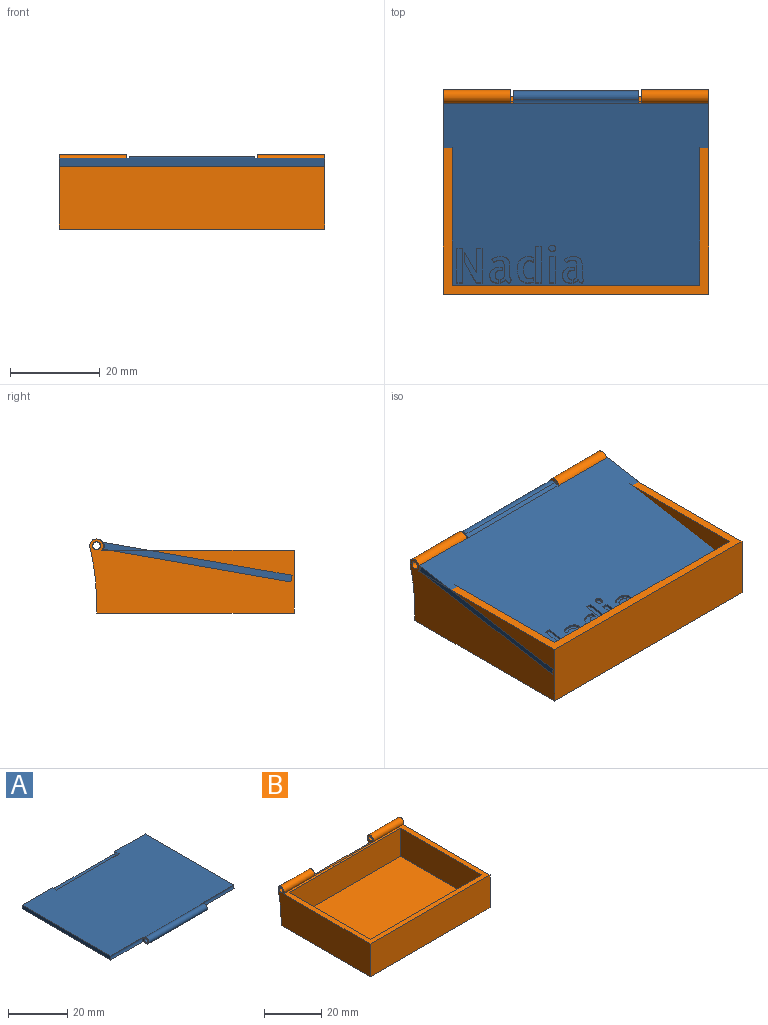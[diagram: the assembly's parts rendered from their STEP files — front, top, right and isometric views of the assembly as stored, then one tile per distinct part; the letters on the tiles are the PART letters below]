
ASSEMBLY  parts=2 mates=1
PART A: 187 faces, bbox 59x45.3x2.5 mm
  f0: plane 59x42.85mm, normal (0,0,1), area 2451.9mm2, adj f2,f4,f5,f6,f7,f8,f9,f10
  f1: plane 59x42.56mm, normal (0,0,-1), area 2423.8mm2, adj f2,f5,f6,f9,f10,f11,f12,f13
  f2: plane 42.56x1.5mm, normal (1,0,0), area 63.5mm2, adj f0,f1,f6,f10
  f3: cylinder r=0.82mm len=28mm, axis (-1,0,0), area 145.1mm2, adj f7,f8
  f4: cylinder r=1.25mm len=28mm, axis (-1,0,0), area 162.6mm2, adj f0,f7,f8,f186
  f5: plane 42.56x1.5mm, normal (-1,0,0), area 63.5mm2, adj f0,f1,f6,f9
  f6: plane 59x1.5mm, normal (0,1,0), area 66.6mm2, adj f0,f1,f2,f5,f182,f183,f185
  f7: plane 3x2.5mm, normal (-1,0,0), area 3.6mm2, adj f0,f3,f4,f9,f186
  f8: plane 3x2.5mm, normal (1,0,0), area 3.6mm2, adj f0,f3,f4,f10,f186
  f9: cylinder r=1.75mm len=15.5mm, axis (1,0,0), area 24.4mm2, adj f0,f1,f5,f7
  f10: cylinder r=1.75mm len=15.5mm, axis (-1,0,0), area 24.4mm2, adj f0,f1,f2,f8
  f11: plane 1.29x0.5mm, normal (0,1,0), area 0.6mm2, adj f1,f12,f17,f18
  f12: plane 5.36x0.5mm, normal (1,0,0), area 2.7mm2, adj f1,f11,f13,f18
  f13: plane 4.61x2.62mm, normal (-0.87,0.49,0), area 2.7mm2, adj f1,f12,f14,f18
  f14: plane 2.43x0.5mm, normal (1,0,0), area 1.2mm2, adj f1,f13,f15,f18
  f15: plane 4.6x2.62mm, normal (0.87,-0.49,0), area 2.6mm2, adj f1,f14,f16,f18
  f16: plane 1.29x0.5mm, normal (0,-1,0), area 0.6mm2, adj f1,f15,f17,f18
  f17: plane 7.78x0.5mm, normal (-1,0,0), area 3.9mm2, adj f1,f11,f16,f18
  f18: plane 7.78x3.9mm, normal (0,0,-1), area 16.3mm2, adj f11,f12,f13,f14,f15,f16,f17
  f19: extruded ~0.5x0.25mm, area 0.1mm2, adj f1,f20,f53,f54
  f20: plane 1.46x0.5mm, normal (-1,0,0), area 0.7mm2, adj f1,f19,f21,f54
  f21: extruded ~0.74x0.5mm, area 0.4mm2, adj f1,f20,f22,f54
  f22: extruded ~0.74x0.5mm, area 0.4mm2, adj f1,f21,f23,f54
  f23: extruded ~0.62x0.5mm, area 0.3mm2, adj f1,f22,f24,f54
  f24: extruded ~0.5x0.43mm, area 0.3mm2, adj f1,f23,f25,f54
  f25: extruded ~0.55x0.5mm, area 0.3mm2, adj f1,f24,f26,f54
  f26: extruded ~0.62x0.5mm, area 0.3mm2, adj f1,f25,f27,f54
  f27: extruded ~0.67x0.5mm, area 0.3mm2, adj f1,f26,f28,f54
  f28: extruded ~0.6x0.5mm, area 0.3mm2, adj f1,f27,f29,f54
  f29: extruded ~0.5x0.49mm, area 0.3mm2, adj f1,f28,f30,f54
  f30: extruded ~0.5x0.32mm, area 0.2mm2, adj f1,f29,f31,f54
  f31: plane 0.73x0.5mm, normal (0.84,-0.55,0), area 0.4mm2, adj f1,f30,f32,f54
  f32: extruded ~0.5x0.2mm, area 0.1mm2, adj f1,f31,f33,f54
  f33: extruded ~0.5x0.31mm, area 0.2mm2, adj f1,f32,f34,f54
  f34: extruded ~0.5x0.38mm, area 0.2mm2, adj f1,f33,f35,f54
  f35: extruded ~0.5x0.44mm, area 0.2mm2, adj f1,f34,f36,f54
  f36: extruded ~0.5x0.44mm, area 0.2mm2, adj f1,f35,f37,f54
  f37: extruded ~0.5x0.31mm, area 0.2mm2, adj f1,f36,f38,f54
  f38: extruded ~0.5x0.45mm, area 0.2mm2, adj f1,f37,f39,f54
  f39: extruded ~0.82x0.5mm, area 0.4mm2, adj f1,f38,f40,f54
  f40: plane 2.23x0.5mm, normal (1,0,0), area 1.1mm2, adj f1,f39,f41,f54
  f41: extruded ~0.5x0.36mm, area 0.3mm2, adj f1,f40,f42,f54
  f42: extruded ~0.5x0.46mm, area 0.3mm2, adj f1,f41,f43,f54
  f43: plane 0.8x0.5mm, normal (1,0,0), area 0.4mm2, adj f1,f42,f44,f54
  f44: extruded ~0.69x0.5mm, area 0.4mm2, adj f1,f43,f45,f54
  f45: extruded ~0.5x0.47mm, area 0.3mm2, adj f1,f44,f46,f54
  f46: extruded ~0.5x0.31mm, area 0.2mm2, adj f1,f45,f47,f54
  f47: extruded ~0.5x0.26mm, area 0.2mm2, adj f1,f46,f48,f54
  f48: extruded ~0.5x0.3mm, area 0.2mm2, adj f1,f47,f49,f54
  f49: extruded ~0.5x0.29mm, area 0.1mm2, adj f1,f48,f50,f54
  f50: plane 0.71x0.5mm, normal (-0.9,-0.43,0), area 0.4mm2, adj f1,f49,f51,f54
  f51: extruded ~0.5x0.19mm, area 0.1mm2, adj f1,f50,f52,f54
  f52: extruded ~0.5x0.31mm, area 0.2mm2, adj f1,f51,f53,f54
  f53: extruded ~0.5x0.33mm, area 0.2mm2, adj f1,f19,f52,f54
  f54: plane 6x4.39mm, normal (0,0,-1), area 9.9mm2, adj f19,f20,f21,f22,f23,f24,f25,f26
  f55: plane 8.2x0.5mm, normal (-1,0,0), area 4.1mm2, adj f1,f56,f59,f60
  f56: plane 1.29x0.5mm, normal (0,1,0), area 0.6mm2, adj f1,f55,f57,f60
  f57: plane 7.49x0.5mm, normal (1,0,0), area 3.7mm2, adj f1,f56,f58,f60
  f58: plane 0.71x0.5mm, normal (0.99,-0.1,0), area 0.4mm2, adj f1,f57,f59,f60
  f59: plane 1.21x0.5mm, normal (0,-1,0), area 0.6mm2, adj f1,f55,f58,f60
  f60: plane 8.2x1.29mm, normal (0,0,-1), area 10.5mm2, adj f55,f56,f57,f58,f59
  f61: extruded ~0.5x0.25mm, area 0.1mm2, adj f1,f62,f95,f96
  f62: plane 1.46x0.5mm, normal (-1,0,0), area 0.7mm2, adj f1,f61,f63,f96
  f63: extruded ~0.74x0.5mm, area 0.4mm2, adj f1,f62,f64,f96
  f64: extruded ~0.74x0.5mm, area 0.4mm2, adj f1,f63,f65,f96
  f65: extruded ~0.62x0.5mm, area 0.3mm2, adj f1,f64,f66,f96
  f66: extruded ~0.5x0.43mm, area 0.3mm2, adj f1,f65,f67,f96
  f67: extruded ~0.55x0.5mm, area 0.3mm2, adj f1,f66,f68,f96
  f68: extruded ~0.62x0.5mm, area 0.3mm2, adj f1,f67,f69,f96
  f69: extruded ~0.67x0.5mm, area 0.3mm2, adj f1,f68,f70,f96
  f70: extruded ~0.6x0.5mm, area 0.3mm2, adj f1,f69,f71,f96
  f71: extruded ~0.5x0.49mm, area 0.3mm2, adj f1,f70,f72,f96
  f72: extruded ~0.5x0.32mm, area 0.2mm2, adj f1,f71,f73,f96
  f73: plane 0.73x0.5mm, normal (0.84,-0.55,0), area 0.4mm2, adj f1,f72,f74,f96
  f74: extruded ~0.5x0.2mm, area 0.1mm2, adj f1,f73,f75,f96
  f75: extruded ~0.5x0.31mm, area 0.2mm2, adj f1,f74,f76,f96
  f76: extruded ~0.5x0.38mm, area 0.2mm2, adj f1,f75,f77,f96
  f77: extruded ~0.5x0.44mm, area 0.2mm2, adj f1,f76,f78,f96
  f78: extruded ~0.5x0.44mm, area 0.2mm2, adj f1,f77,f79,f96
  f79: extruded ~0.5x0.31mm, area 0.2mm2, adj f1,f78,f80,f96
  f80: extruded ~0.5x0.45mm, area 0.2mm2, adj f1,f79,f81,f96
  f81: extruded ~0.82x0.5mm, area 0.4mm2, adj f1,f80,f82,f96
  f82: plane 2.23x0.5mm, normal (1,0,0), area 1.1mm2, adj f1,f81,f83,f96
  f83: extruded ~0.5x0.36mm, area 0.3mm2, adj f1,f82,f84,f96
  f84: extruded ~0.5x0.46mm, area 0.3mm2, adj f1,f83,f85,f96
  f85: plane 0.8x0.5mm, normal (1,0,0), area 0.4mm2, adj f1,f84,f86,f96
  f86: extruded ~0.69x0.5mm, area 0.4mm2, adj f1,f85,f87,f96
  f87: extruded ~0.5x0.47mm, area 0.3mm2, adj f1,f86,f88,f96
  f88: extruded ~0.5x0.31mm, area 0.2mm2, adj f1,f87,f89,f96
  f89: extruded ~0.5x0.26mm, area 0.2mm2, adj f1,f88,f90,f96
  f90: extruded ~0.5x0.3mm, area 0.2mm2, adj f1,f89,f91,f96
  f91: extruded ~0.5x0.29mm, area 0.1mm2, adj f1,f90,f92,f96
  f92: plane 0.71x0.5mm, normal (-0.9,-0.43,0), area 0.4mm2, adj f1,f91,f93,f96
  f93: extruded ~0.5x0.19mm, area 0.1mm2, adj f1,f92,f94,f96
  f94: extruded ~0.5x0.31mm, area 0.2mm2, adj f1,f93,f95,f96
  f95: extruded ~0.5x0.33mm, area 0.2mm2, adj f1,f61,f94,f96
  f96: plane 6x4.39mm, normal (0,0,-1), area 9.9mm2, adj f61,f62,f63,f64,f65,f66,f67,f68
  f97: extruded ~0.71x0.5mm, area 0.4mm2, adj f1,f98,f115,f116
  f98: extruded ~0.55x0.5mm, area 0.3mm2, adj f1,f97,f99,f116
  f99: extruded ~0.5x0.33mm, area 0.2mm2, adj f1,f98,f100,f116
  f100: extruded ~0.5x0.43mm, area 0.2mm2, adj f1,f99,f101,f116
  f101: extruded ~0.5x0.44mm, area 0.2mm2, adj f1,f100,f102,f116
  f102: plane 0.5x0.23mm, normal (0,-1,0), area 0.1mm2, adj f1,f101,f103,f116
  f103: plane 0.75x0.5mm, normal (-1,0,0), area 0.4mm2, adj f1,f102,f104,f116
  f104: plane 0.5x0.46mm, normal (0,1,0), area 0.2mm2, adj f1,f103,f105,f116
  f105: extruded ~0.83x0.5mm, area 0.4mm2, adj f1,f104,f106,f116
  f106: extruded ~0.73x0.5mm, area 0.4mm2, adj f1,f105,f107,f116
  f107: extruded ~0.58x0.53mm, area 0.4mm2, adj f1,f106,f108,f116
  f108: extruded ~0.84x0.5mm, area 0.4mm2, adj f1,f107,f109,f116
  f109: extruded ~0.86x0.5mm, area 0.4mm2, adj f1,f108,f110,f116
  f110: extruded ~0.56x0.5mm, area 0.3mm2, adj f1,f109,f111,f116
  f111: extruded ~0.59x0.5mm, area 0.3mm2, adj f1,f110,f112,f116
  f112: extruded ~0.69x0.5mm, area 0.3mm2, adj f1,f111,f113,f116
  f113: extruded ~0.5x0.14mm, area 0.1mm2, adj f1,f112,f114,f116
  f114: plane 0.85x0.5mm, normal (-1,0,0), area 0.4mm2, adj f1,f113,f115,f116
  f115: extruded ~0.56x0.5mm, area 0.3mm2, adj f1,f97,f114,f116
  f116: plane 3.68x2.76mm, normal (0,0,-1), area 5.2mm2, adj f97,f98,f99,f100,f101,f102,f103,f104
  f117: plane 7.78x0.5mm, normal (1,0,0), area 3.9mm2, adj f1,f118,f120,f121
  f118: plane 1.29x0.5mm, normal (0,-1,0), area 0.6mm2, adj f1,f117,f119,f121
  f119: plane 7.78x0.5mm, normal (-1,0,0), area 3.9mm2, adj f1,f118,f120,f121
  f120: plane 1.29x0.5mm, normal (0,1,0), area 0.6mm2, adj f1,f117,f119,f121
  f121: plane 7.78x1.29mm, normal (0,0,-1), area 10mm2, adj f117,f118,f119,f120
  f122: extruded ~0.71x0.5mm, area 0.4mm2, adj f1,f123,f140,f141
  f123: extruded ~0.55x0.5mm, area 0.3mm2, adj f1,f122,f124,f141
  f124: extruded ~0.5x0.33mm, area 0.2mm2, adj f1,f123,f125,f141
  f125: extruded ~0.5x0.43mm, area 0.2mm2, adj f1,f124,f126,f141
  f126: extruded ~0.5x0.44mm, area 0.2mm2, adj f1,f125,f127,f141
  f127: plane 0.5x0.23mm, normal (0,-1,0), area 0.1mm2, adj f1,f126,f128,f141
  f128: plane 0.75x0.5mm, normal (-1,0,0), area 0.4mm2, adj f1,f127,f129,f141
  f129: plane 0.5x0.46mm, normal (0,1,0), area 0.2mm2, adj f1,f128,f130,f141
  f130: extruded ~0.83x0.5mm, area 0.4mm2, adj f1,f129,f131,f141
  f131: extruded ~0.73x0.5mm, area 0.4mm2, adj f1,f130,f132,f141
  f132: extruded ~0.58x0.53mm, area 0.4mm2, adj f1,f131,f133,f141
  f133: extruded ~0.84x0.5mm, area 0.4mm2, adj f1,f132,f134,f141
  f134: extruded ~0.86x0.5mm, area 0.4mm2, adj f1,f133,f135,f141
  f135: extruded ~0.56x0.5mm, area 0.3mm2, adj f1,f134,f136,f141
  f136: extruded ~0.59x0.5mm, area 0.3mm2, adj f1,f135,f137,f141
  f137: extruded ~0.69x0.5mm, area 0.3mm2, adj f1,f136,f138,f141
  f138: extruded ~0.5x0.14mm, area 0.1mm2, adj f1,f137,f139,f141
  f139: plane 0.85x0.5mm, normal (-1,0,0), area 0.4mm2, adj f1,f138,f140,f141
  f140: extruded ~0.56x0.5mm, area 0.3mm2, adj f1,f122,f139,f141
  f141: plane 3.68x2.76mm, normal (0,0,-1), area 5.2mm2, adj f122,f123,f124,f125,f126,f127,f128,f129
  f142: extruded ~0.53x0.5mm, area 0.3mm2, adj f1,f143,f149,f150
  f143: extruded ~0.54x0.5mm, area 0.3mm2, adj f1,f142,f144,f150
  f144: extruded ~0.54x0.5mm, area 0.3mm2, adj f1,f143,f145,f150
  f145: extruded ~0.53x0.5mm, area 0.3mm2, adj f1,f144,f146,f150
  f146: extruded ~0.54x0.5mm, area 0.3mm2, adj f1,f145,f147,f150
  f147: extruded ~0.53x0.5mm, area 0.3mm2, adj f1,f146,f148,f150
  f148: extruded ~0.53x0.5mm, area 0.3mm2, adj f1,f147,f149,f150
  f149: extruded ~0.54x0.5mm, area 0.3mm2, adj f1,f142,f148,f150
  f150: plane 1.51x1.51mm, normal (0,0,-1), area 1.8mm2, adj f142,f143,f144,f145,f146,f147,f148,f149
  f151: plane 1.29x0.5mm, normal (0,-1,0), area 0.6mm2, adj f1,f152,f154,f155
  f152: plane 5.95x0.5mm, normal (-1,0,0), area 3mm2, adj f1,f151,f153,f155
  f153: plane 1.29x0.5mm, normal (0,1,0), area 0.6mm2, adj f1,f152,f154,f155
  f154: plane 5.95x0.5mm, normal (1,0,0), area 3mm2, adj f1,f151,f153,f155
  f155: plane 5.95x1.29mm, normal (0,0,-1), area 7.7mm2, adj f151,f152,f153,f154
  f156: extruded ~1.38x0.5mm, area 0.7mm2, adj f1,f157,f180,f181
  f157: extruded ~1.34x0.5mm, area 0.7mm2, adj f1,f156,f158,f181
  f158: extruded ~1.12x0.59mm, area 0.6mm2, adj f1,f157,f159,f181
  f159: extruded ~0.72x0.5mm, area 0.4mm2, adj f1,f158,f160,f181
  f160: extruded ~0.83x0.5mm, area 0.4mm2, adj f1,f159,f161,f181
  f161: extruded ~0.7x0.5mm, area 0.4mm2, adj f1,f160,f162,f181
  f162: extruded ~0.59x0.5mm, area 0.3mm2, adj f1,f161,f163,f181
  f163: plane 1.1x0.5mm, normal (-1,0,0), area 0.5mm2, adj f1,f162,f164,f181
  f164: extruded ~0.87x0.5mm, area 0.5mm2, adj f1,f163,f165,f181
  f165: extruded ~0.57x0.5mm, area 0.3mm2, adj f1,f164,f166,f181
  f166: extruded ~0.5x0.44mm, area 0.3mm2, adj f1,f165,f167,f181
  f167: extruded ~0.64x0.5mm, area 0.4mm2, adj f1,f166,f168,f181
  f168: extruded ~0.79x0.5mm, area 0.4mm2, adj f1,f167,f169,f181
  f169: extruded ~0.79x0.5mm, area 0.4mm2, adj f1,f168,f170,f181
  f170: extruded ~0.65x0.5mm, area 0.4mm2, adj f1,f169,f171,f181
  f171: extruded ~0.5x0.45mm, area 0.3mm2, adj f1,f170,f172,f181
  f172: extruded ~0.58x0.5mm, area 0.3mm2, adj f1,f171,f173,f181
  f173: extruded ~0.5x0.5mm, area 0.3mm2, adj f1,f172,f174,f181
  f174: extruded ~0.5x0.4mm, area 0.3mm2, adj f1,f173,f175,f181
  f175: plane 1.12x0.5mm, normal (-1,0,0), area 0.6mm2, adj f1,f174,f176,f181
  f176: extruded ~0.53x0.5mm, area 0.3mm2, adj f1,f175,f177,f181
  f177: extruded ~0.62x0.5mm, area 0.3mm2, adj f1,f176,f178,f181
  f178: extruded ~0.86x0.5mm, area 0.4mm2, adj f1,f177,f179,f181
  f179: extruded ~0.8x0.5mm, area 0.5mm2, adj f1,f178,f180,f181
  f180: extruded ~0.91x0.59mm, area 0.5mm2, adj f1,f156,f179,f181
  f181: plane 6.06x3.62mm, normal (0,0,-1), area 11mm2, adj f156,f157,f158,f159,f160,f161,f162,f163
  f182: plane 28.5x1.25mm, normal (0,0,1), area 35.6mm2, adj f6,f183,f184,f185
  f183: plane 2x0.75mm, normal (-0.71,0,0.71), area 1.7mm2, adj f0,f6,f182,f184
  f184: plane 30x0.75mm, normal (0,0.71,0.71), area 31mm2, adj f0,f182,f183,f185
  f185: plane 2x0.75mm, normal (0.71,0,0.71), area 1.7mm2, adj f0,f6,f182,f184
  f186: cylinder r=3mm len=28mm, axis (-1,0,0), area 29mm2, adj f1,f4,f7,f8
PART B: 20 faces, bbox 59x45.5x16.5 mm
  f0: cylinder r=1.5mm len=15mm, axis (1,0,0), area 92.5mm2, adj f2,f5,f16,f19
  f1: cylinder r=0.88mm len=15mm, axis (1,0,0), area 82.5mm2, adj f3,f15
  f2: plane 59x42.88mm, normal (0,0,1), area 330mm2, adj f0,f3,f4,f5,f8,f9,f10,f11
  f3: plane 45.5x16.5mm, normal (-1,0,0), area 624.8mm2, adj f1,f2,f4,f6,f7,f13,f18
  f4: plane 59x14mm, normal (0,-1,0), area 826mm2, adj f2,f3,f5,f7
  f5: plane 45.5x16.5mm, normal (1,0,0), area 624.8mm2, adj f0,f2,f4,f6,f7,f14,f19
  f6: plane 59x13.5mm, normal (0,1,0), area 471.3mm2, adj f3,f5,f7,f15,f16,f17,f18,f19
  f7: plane 59x44mm, normal (0,0,-1), area 2596mm2, adj f3,f4,f5,f6
  f8: plane 40x12mm, normal (1,0,0), area 480mm2, adj f2,f9,f11,f12
  f9: plane 55x12mm, normal (0,1,0), area 660mm2, adj f2,f8,f10,f12
  f10: plane 40x12mm, normal (-1,0,0), area 480mm2, adj f2,f9,f11,f12
  f11: plane 55x12mm, normal (0,-1,0), area 660mm2, adj f2,f8,f10,f12
  f12: plane 55x40mm, normal (0,0,1), area 2200mm2, adj f8,f9,f10,f11
  f13: cylinder r=1.5mm len=15mm, axis (1,0,0), area 92.5mm2, adj f2,f3,f15,f18
  f14: cylinder r=0.88mm len=15mm, axis (1,0,0), area 82.5mm2, adj f5,f16
  f15: plane 13.84x3mm, normal (1,0,0), area 9.2mm2, adj f1,f6,f13,f17,f18
  f16: plane 13.84x3mm, normal (-1,0,0), area 9.2mm2, adj f0,f6,f14,f17,f19
  f17: cylinder r=1.5mm len=29mm, axis (1,0,0), area 36.6mm2, adj f2,f6,f15,f16
  f18: cylinder r=50mm len=15mm, axis (1,0,0), area 181.5mm2, adj f3,f6,f13,f15
  f19: cylinder r=50mm len=15mm, axis (1,0,0), area 181.5mm2, adj f0,f5,f6,f16
PLACE A rot(axis=(-1,0,0),170.1deg) t=(60.68,20.46,6.96)mm
PLACE B t=(-17.89,22.69,-0.97)mm fixed
MATE revolute A.f3 <-> B.f0  axis (-1,0,0) through (25.61,66.69,14.03)mm
